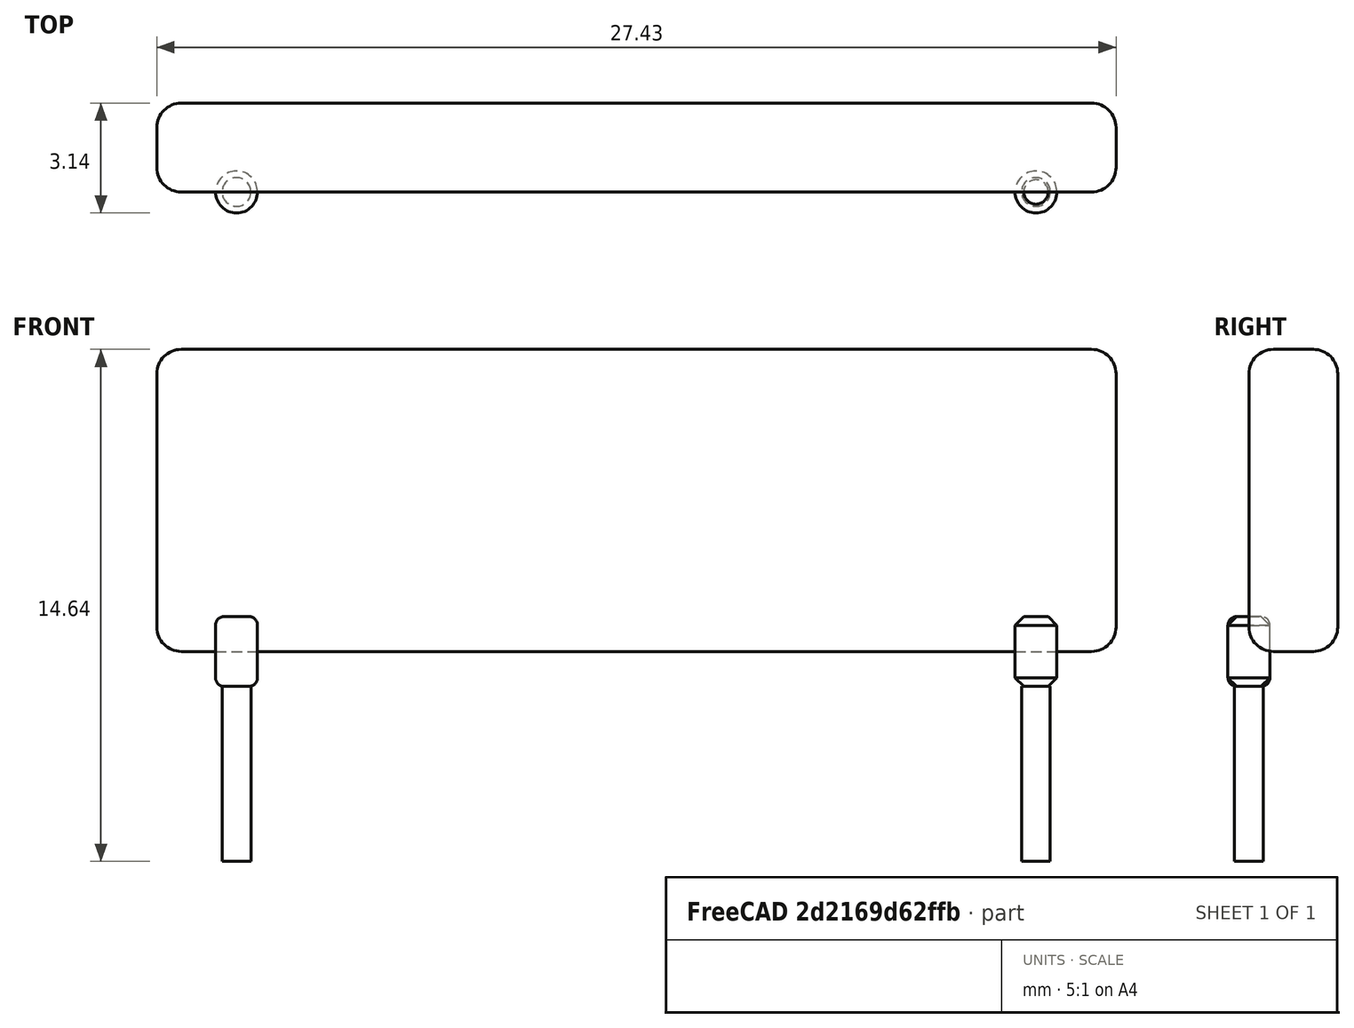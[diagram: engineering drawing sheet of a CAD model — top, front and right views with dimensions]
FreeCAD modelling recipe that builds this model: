
FCSTD DOCUMENT
Label: slim_mox
objects: Part::Feature×5, Part::Cylinder×4, Part::Fillet×2, Part::Chamfer×1, Part::Box×1
note: 13 computed .brp shape members not serialized (recipe doc carries the construction recipe); baked Part::Feature solids carry a one-line shape summary decoded from their .brp

FEATURE [Part::Cylinder] Cylinder
  Angle = 360
  Height = 5
  Radius = 0.41
FEATURE [Part::Cylinder] Cylinder001
  Angle = 360
  Height = 5
  Placement = pos=(22.86,0,0) rot=(0,0,1;0rad)
  Radius = 0.41
FEATURE [Part::Cylinder] Cylinder002
  Angle = 360
  Height = 2
  Placement = pos=(0,0,5) rot=(0,0,1;0rad)
  Radius = 0.6
FEATURE [Part::Cylinder] Cylinder003
  Angle = 360
  Height = 2
  Placement = pos=(22.86,0,5) rot=(0,0,1;0rad)
  Radius = 0.6
FEATURE [Part::Fillet] Fillet
  Base = -> Cylinder002
  Edges = 2 edges r=0.25: [Edge1,Edge3]
FEATURE [Part::Chamfer] Chamfer
  Base = -> Cylinder003
  Edges = 2 edges r=0.25: [Edge1,Edge3]
FEATURE [Part::Box] Box
  Height = 8.64
  Length = 27.43
  Placement = pos=(-2.28,0,6) rot=(0,0,1;0rad)
  Width = 2.54
FEATURE [Part::Fillet] Fillet001
  Base = -> Box
  Edges = 12 edges r=0.7: [Edge1,Edge2,Edge3,Edge4,Edge5,Edge6,Edge7,Edge8,Edge9,Edge10,Edge11,Edge12]
FEATURE [Part::Feature] Cylinder004
  shape: bbox 0.82 x 0.82 x 5 mm, 3 faces (baked)
FEATURE [Part::Feature] Cylinder001001  label="Cylinder005"
  Placement = pos=(22.86,0,0) rot=(0,0,1;0rad)
  shape: bbox 0.82 x 0.82 x 5 mm, 3 faces (baked)
FEATURE [Part::Feature] Fillet002
  shape: bbox 1.299 x 1.299 x 2 mm, 5 faces (baked)
FEATURE [Part::Feature] Chamfer001
  shape: bbox 1.2 x 1.2 x 2 mm, 5 faces (baked)
FEATURE [Part::Feature] Fillet001001  label="Fillet003"
  shape: bbox 27.43 x 2.54 x 8.64 mm, 26 faces (baked)
